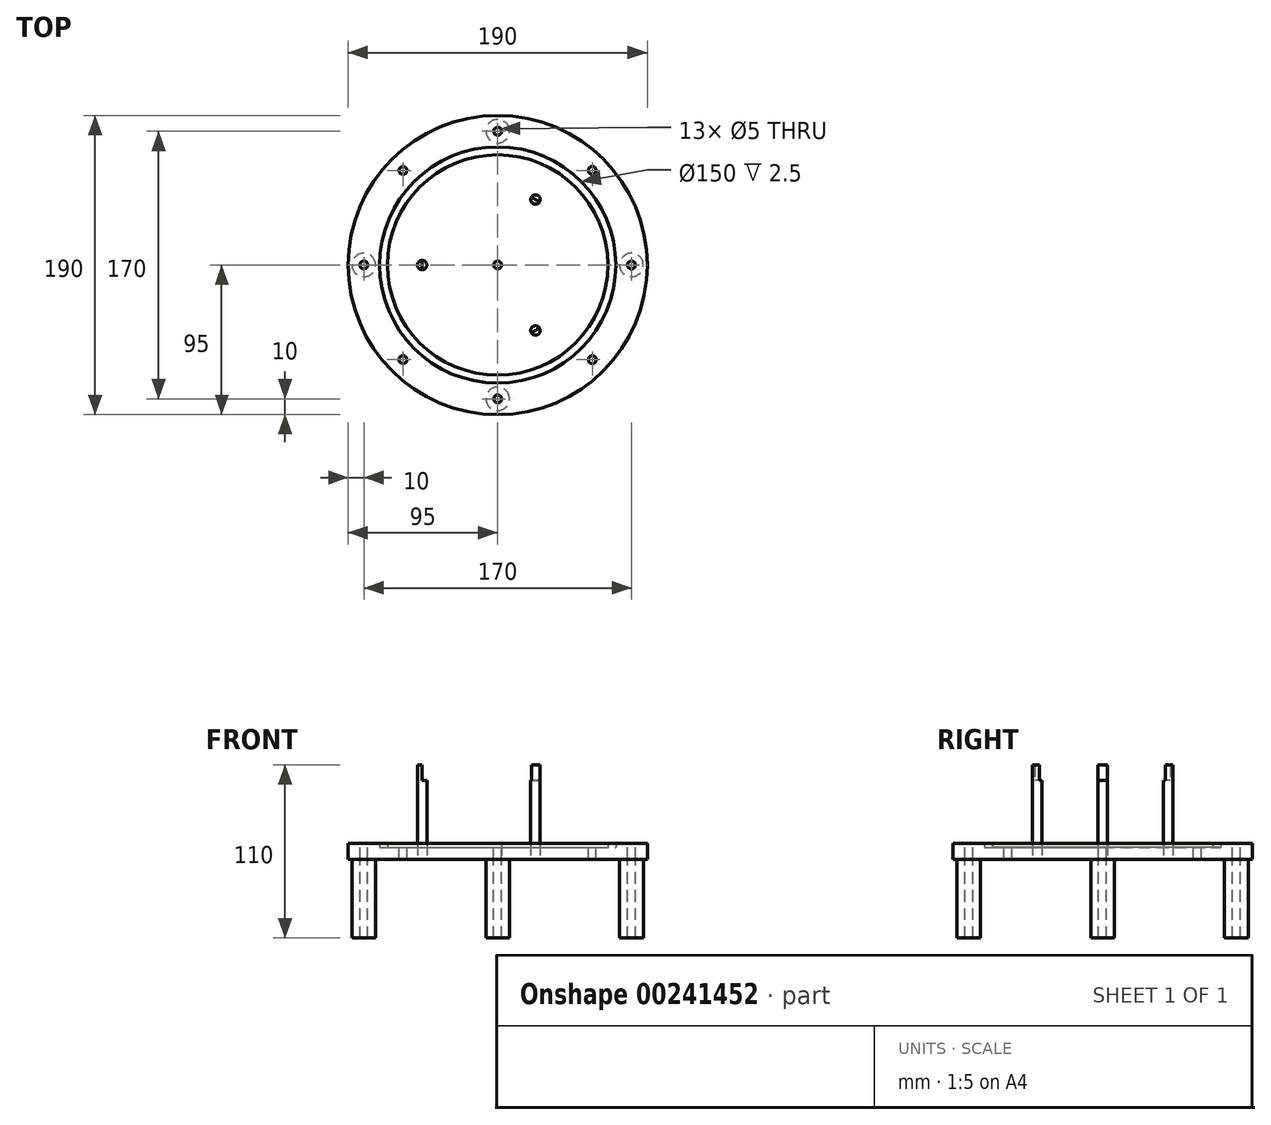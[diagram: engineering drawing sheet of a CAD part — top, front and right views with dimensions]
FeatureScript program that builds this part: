
annotation { "Feature Type Name" : "Feature", "Feature Type Description" : "" }
export const myFeature = defineFeature(function(context is Context, id is Id, definition is map)
    precondition{}
    {
        {
            var Q0;
            Q0=qCreatedBy(makeId("Front.planeOp"),FACE);
            var sketch = newSketch(context, id + "F0", { "sketchPlane" : qUnion([Q0])});
            skLineSegment(sketch, "E0", {"start": v(0, 0) * mm, "end": v(0, 66.09) * mm});
            skSolve(sketch);
        }
        {
            var Q0;
            Q0=qCreatedBy(makeId("Top.planeOp"),FACE);
            var sketch = newSketch(context, id + "F1", { "sketchPlane" : qUnion([Q0])});
            skCircle(sketch, "E1", {"center": v(0, 0) * mm, "radius": 95 * mm});
            skCircle(sketch, "E2.0", {"center": v(0, 0) * mm, "radius": 65 * mm});
            skCircle(sketch, "E3", {"center": v(0, 0) * mm, "radius": 62 * mm});
            skCircle(sketch, "E4", {"center": v(0, 0) * mm, "radius": 48 * mm});
            skCircle(sketch, "E5", {"center": v(0, 0) * mm, "radius": 45 * mm});
            skSolve(sketch);
        }
        {
            var Q0;
            Q0=qSketchRegion(id+"F1",true);
            var Q1;
            Q1=makeQuery(id+"F1.imprint","IMPRINT",FACE,{"disambiguationData":[TD([[makeQuery(id+"F1.imprint","IMPRINT",EDGE,{"derivedFrom":sQuery(id+"F1.wireOp",EDGE,"E5")}),1.0]])]});
            var Q2;
            Q2=makeQuery(id+"F1.imprint","IMPRINT",FACE,{"disambiguationData":[TD([[makeQuery(id+"F1.imprint","IMPRINT",EDGE,{"derivedFrom":sQuery(id+"F1.wireOp",EDGE,"E4")}),1.0]])]});
            var Q3;
            Q3=makeQuery(id+"F1.imprint","IMPRINT",FACE,{"disambiguationData":[TD([[makeQuery(id+"F1.imprint","IMPRINT",EDGE,{"derivedFrom":sQuery(id+"F1.wireOp",EDGE,"E3")}),1.0]])]});
            var Q4;
            Q4=makeQuery(id+"F1.imprint","IMPRINT",FACE,{"disambiguationData":[TD([[makeQuery(id+"F1.imprint","IMPRINT",EDGE,{"derivedFrom":sQuery(id+"F1.wireOp",EDGE,"E2.0")}),1.0]])]});
            extrude(context, id + "F2", {"entities" : qUnion([Q0, Q1, Q2, Q3, Q4]), "depth" : 10 * mm});
        }
        {
            var Q0;
            Q0=qCreatedBy(makeId("Top.planeOp"),FACE);
            cPlane(context, id + "F3", {"entities" : qUnion([Q0]), "cplaneType" : CPlaneType.OFFSET, "offset" : 10 * mm, "width" : 150 * mm, "height" : 150 * mm});
        }
        {
            var Q0;
            Q0=qCreatedBy(makeId("Front.planeOp"),FACE);
            var sketch = newSketch(context, id + "F4", { "sketchPlane" : qUnion([Q0])});
            skLineSegment(sketch, "E6.bottom", {"start": v(-70, 7.5) * mm, "end": v(-75, 7.5) * mm});
            skLineSegment(sketch, "E6.top", {"start": v(-70, 12.5) * mm, "end": v(-75, 12.5) * mm});
            skLineSegment(sketch, "E6.left", {"start": v(-70, 7.5) * mm, "end": v(-70, 12.5) * mm});
            skLineSegment(sketch, "E6.right", {"start": v(-75, 7.5) * mm, "end": v(-75, 12.5) * mm});
            skPoint(sketch, "E6.middle", {"position": v(-72.5, 10) * mm});
            skSolve(sketch);
        }
        {
            var Q0;
            Q0=makeQuery(id+"F4.imprint","IMPRINT",FACE,{"disambiguationData":[TD([[makeQuery(id+"F4.imprint","IMPRINT",EDGE,{"derivedFrom":sQuery(id+"F4.wireOp",EDGE,"E6.bottom")}),-1.0]])]});
            var Q1;
            Q1=makeQuery(id+"F2.opExtrude","CAP_EDGE",EDGE,{"disambiguationData":[OSD([sQuery(id+"F1.wireOp",EDGE,"E1")])],"isStart":false});
            revolve(context, id + "F5", {"operationType" : NewBodyOperationType.REMOVE, "entities" : qUnion([Q0]), "axis" : qUnion([Q1]), "revolveType" : RevolveType.FULL});
        }
        {
            var Q0;
            Q0=qCreatedBy(id+"F3.planeOp",FACE);
            var sketch = newSketch(context, id + "F6", { "sketchPlane" : qUnion([Q0])});
            skCircle(sketch, "E7", {"center": v(-85, 0) * mm, "radius": 2.5 * mm});
            skSolve(sketch);
        }
        {
            var Q0;
            Q0=makeQuery(id+"F6.imprint","IMPRINT",FACE,{"disambiguationData":[TD([[makeQuery(id+"F6.imprint","IMPRINT",EDGE,{"derivedFrom":sQuery(id+"F6.wireOp",EDGE,"E7")}),1.0]])]});
            extrude(context, id + "F7", {"entities" : qUnion([Q0]), "oppositeDirection" : true, "depth" : 10 * mm});
        }
        {
            var Q0;
            Q0=makeQuery(id+"F7.opExtrude","SWEPT_BODY",BODY,{"disambiguationData":[OSD([sQuery(id+"F6.wireOp",EDGE,"E7")])]});
            var Q1;
            Q1=sQuery(id+"F0.wireOp",EDGE,"E0");
            circularPattern(context, id + "F8", {"entities" : qUnion([Q0]), "axis" : qUnion([Q1]), "angle" : 360 * degree, "instanceCount" : 8, "equalSpace" : true});
        }
        {
            var Q0;
            Q0=makeQuery(id+"F7.opExtrude","SWEPT_BODY",BODY,{"disambiguationData":[OSD([sQuery(id+"F6.wireOp",EDGE,"E7")])]});
            var Q1;
            Q1=makeQuery(id+"F8.opPattern","COPY",BODY,{"derivedFrom":makeQuery(id+"F7.opExtrude","SWEPT_BODY",BODY,{"disambiguationData":[OSD([sQuery(id+"F6.wireOp",EDGE,"E7")])]}),"instanceName":"7"});
            var Q2;
            Q2=makeQuery(id+"F8.opPattern","COPY",BODY,{"derivedFrom":makeQuery(id+"F7.opExtrude","SWEPT_BODY",BODY,{"disambiguationData":[OSD([sQuery(id+"F6.wireOp",EDGE,"E7")])]}),"instanceName":"6"});
            var Q3;
            Q3=makeQuery(id+"F8.opPattern","COPY",BODY,{"derivedFrom":makeQuery(id+"F7.opExtrude","SWEPT_BODY",BODY,{"disambiguationData":[OSD([sQuery(id+"F6.wireOp",EDGE,"E7")])]}),"instanceName":"5"});
            var Q4;
            Q4=makeQuery(id+"F8.opPattern","COPY",BODY,{"derivedFrom":makeQuery(id+"F7.opExtrude","SWEPT_BODY",BODY,{"disambiguationData":[OSD([sQuery(id+"F6.wireOp",EDGE,"E7")])]}),"instanceName":"4"});
            var Q5;
            Q5=makeQuery(id+"F8.opPattern","COPY",BODY,{"derivedFrom":makeQuery(id+"F7.opExtrude","SWEPT_BODY",BODY,{"disambiguationData":[OSD([sQuery(id+"F6.wireOp",EDGE,"E7")])]}),"instanceName":"3"});
            var Q6;
            Q6=makeQuery(id+"F8.opPattern","COPY",BODY,{"derivedFrom":makeQuery(id+"F7.opExtrude","SWEPT_BODY",BODY,{"disambiguationData":[OSD([sQuery(id+"F6.wireOp",EDGE,"E7")])]}),"instanceName":"2"});
            var Q7;
            Q7=makeQuery(id+"F8.opPattern","COPY",BODY,{"derivedFrom":makeQuery(id+"F7.opExtrude","SWEPT_BODY",BODY,{"disambiguationData":[OSD([sQuery(id+"F6.wireOp",EDGE,"E7")])]}),"instanceName":"1"});
            var Q8;
            Q8=makeQuery(id+"F2.opExtrude","SWEPT_BODY",BODY,{"disambiguationData":[OSD([sQuery(id+"F1.wireOp",EDGE,"E1")])]});
            booleanBodies(context, id + "F9", {"operationType" : BooleanOperationType.SUBTRACTION, "tools" : qUnion([Q0, Q1, Q2, Q3, Q4, Q5, Q6, Q7]), "targets" : qUnion([Q8])});
        }
        {
            var Q0;
            Q0=qCreatedBy(makeId("Top.planeOp"),FACE);
            var sketch = newSketch(context, id + "F10", { "sketchPlane" : qUnion([Q0])});
            skCircle(sketch, "E8", {"center": v(0, 0) * mm, "radius": 2.5 * mm});
            skSolve(sketch);
        }
        {
            var Q0;
            Q0=qSketchRegion(id+"F10",true);
            extrude(context, id + "F11", {"entities" : qUnion([Q0]), "operationType" : NewBodyOperationType.REMOVE, "depth" : 10 * mm});
        }
        {
            var Q0;
            Q0=qCreatedBy(makeId("Top.planeOp"),FACE);
            var sketch = newSketch(context, id + "F12", { "sketchPlane" : qUnion([Q0])});
            skCircle(sketch, "E9", {"center": v(-85, 0) * mm, "radius": 2.5 * mm});
            skCircle(sketch, "E10.0", {"center": v(-85, 0) * mm, "radius": 7.5 * mm});
            skSolve(sketch);
        }
        {
            var Q0;
            Q0=qSketchRegion(id+"F12",true);
            extrude(context, id + "F13", {"entities" : qUnion([Q0]), "oppositeDirection" : true, "depth" : 50 * mm});
        }
        {
            var Q0;
            Q0=makeQuery(id+"F13.opExtrude","SWEPT_BODY",BODY,{"disambiguationData":[OSD([sQuery(id+"F12.wireOp",EDGE,"E9"),sQuery(id+"F12.wireOp",EDGE,"E10.0")])]});
            var Q1;
            Q1=sQuery(id+"F0.wireOp",EDGE,"E0");
            circularPattern(context, id + "F14", {"entities" : qUnion([Q0]), "axis" : qUnion([Q1]), "angle" : 360 * degree, "instanceCount" : 4, "equalSpace" : true});
        }
        {
            var Q0;
            Q0=makeQuery(id+"F1.imprint","IMPRINT",FACE,{"disambiguationData":[TD([[makeQuery(id+"F1.imprint","IMPRINT",EDGE,{"derivedFrom":sQuery(id+"F1.wireOp",EDGE,"E1")}),1.0]])]});
            var sketch = newSketch(context, id + "F15", { "sketchPlane" : qUnion([Q0])});
            skCircle(sketch, "E11", {"center": v(-48, 0) * mm, "radius": 3 * mm});
            skSolve(sketch);
        }
        {
            var Q0;
            Q0=makeQuery(id+"F15.imprint","IMPRINT",FACE,{"disambiguationData":[TD([[makeQuery(id+"F15.imprint","IMPRINT",EDGE,{"derivedFrom":sQuery(id+"F15.wireOp",EDGE,"E11")}),1.0]])]});
            var Q1;
            Q1=sQuery(id+"F15.wireOp",EDGE,"E11");
            extrude(context, id + "F16", {"entities" : qUnion([Q0]), "surfaceEntities" : qUnion([Q1]), "depth" : 60 * mm});
        }
        {
            var Q0;
            Q0=qCreatedBy(makeId("Top.planeOp"),FACE);
            cPlane(context, id + "F17", {"entities" : qUnion([Q0]), "cplaneType" : CPlaneType.OFFSET, "offset" : 50 * mm, "width" : 150 * mm, "height" : 150 * mm});
        }
        {
            var Q0;
            Q0=makeQuery(id+"F16.opExtrude","SWEPT_BODY",BODY,{"disambiguationData":[OSD([sQuery(id+"F15.wireOp",EDGE,"E11")])]});
            var Q1;
            Q1=sQuery(id+"F0.wireOp",EDGE,"E0");
            circularPattern(context, id + "F18", {"entities" : qUnion([Q0]), "axis" : qUnion([Q1]), "angle" : 360 * degree, "instanceCount" : 3, "equalSpace" : true});
        }
        {
            var Q0;
            Q0=qCreatedBy(id+"F17.planeOp",FACE);
            var sketch = newSketch(context, id + "F19", { "sketchPlane" : qUnion([Q0])});
            skCircle(sketch, "E12", {"center": v(0, 0) * mm, "radius": 42 * mm});
            skCircle(sketch, "E13.0", {"center": v(0, 0) * mm, "radius": 48 * mm});
            skSolve(sketch);
        }
        {
            var Q0;
            Q0=qSketchRegion(id+"F19",true);
            extrude(context, id + "F20", {"entities" : qUnion([Q0]), "operationType" : NewBodyOperationType.REMOVE, "depth" : 10 * mm});
        }
    });
